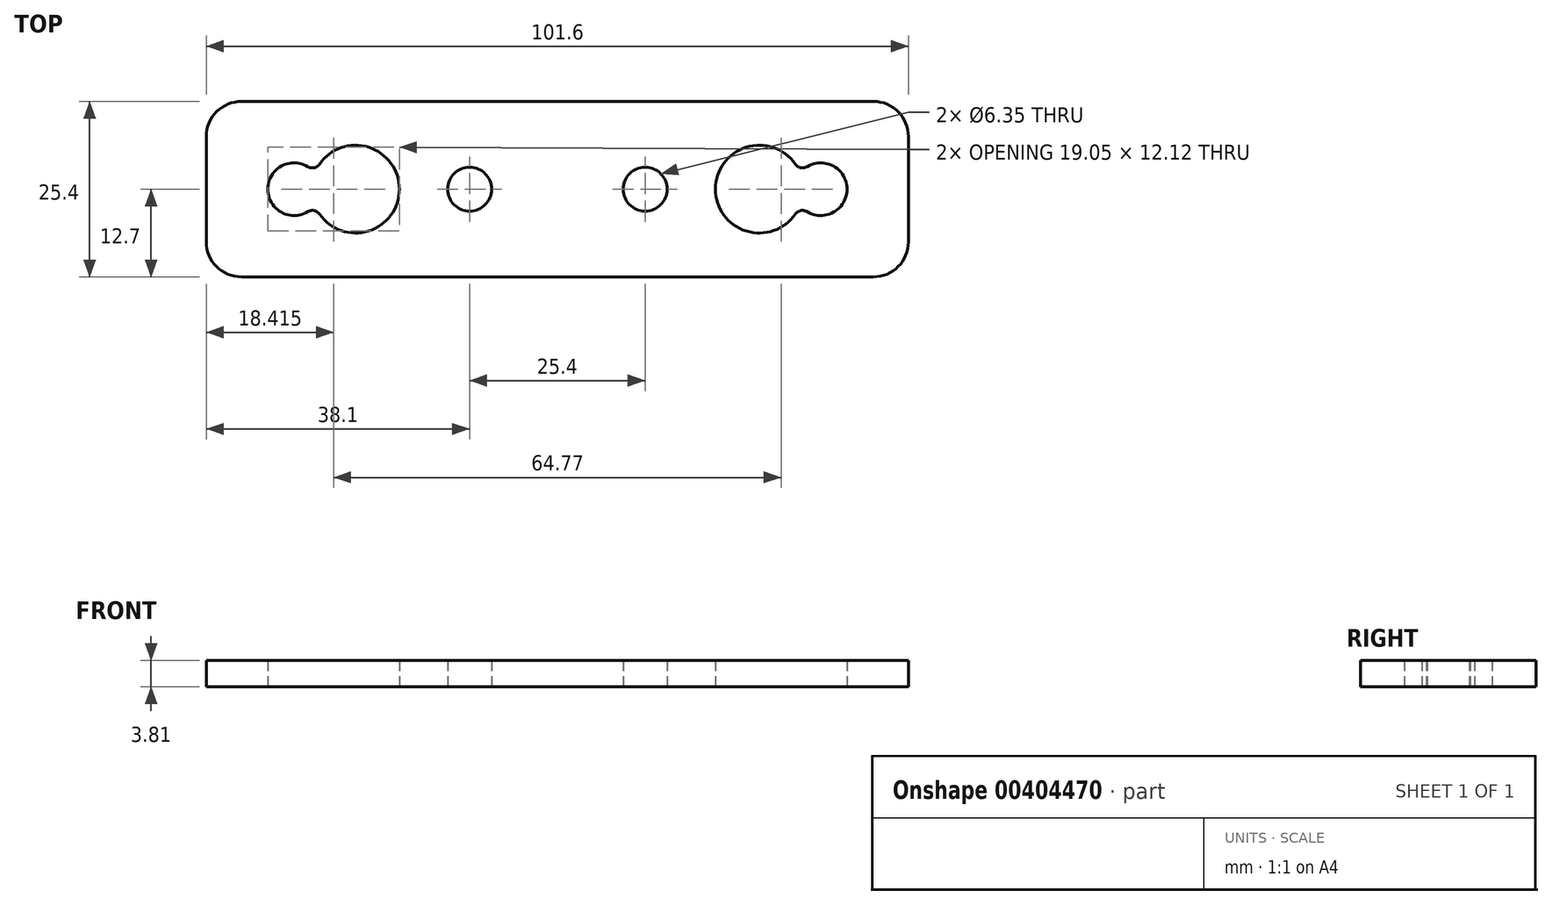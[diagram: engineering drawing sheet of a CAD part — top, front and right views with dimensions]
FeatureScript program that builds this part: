
annotation { "Feature Type Name" : "Feature", "Feature Type Description" : "" }
export const myFeature = defineFeature(function(context is Context, id is Id, definition is map)
    precondition{}
    {
        {
            var Q0;
            Q0=qCreatedBy(makeId("Top.planeOp"),FACE);
            var sketch = newSketch(context, id + "F0", { "sketchPlane" : qUnion([Q0])});
            skLineSegment(sketch, "E0.bottom", {"start": v(-50.8, 12.7) * mm, "end": v(50.8, 12.7) * mm});
            skLineSegment(sketch, "E0.top", {"start": v(-50.8, -12.7) * mm, "end": v(50.8, -12.7) * mm});
            skLineSegment(sketch, "E0.left", {"start": v(-50.8, 12.7) * mm, "end": v(-50.8, -12.7) * mm});
            skLineSegment(sketch, "E0.right", {"start": v(50.8, 12.7) * mm, "end": v(50.8, -12.7) * mm});
            skPoint(sketch, "E0.middle", {"position": v(0, 0) * mm});
            skLineSegment(sketch, "E1", {"start": v(-29.21, 0) * mm, "end": v(29.21, 0) * mm, "construction": true});
            skLineSegment(sketch, "E2", {"start": v(-38.1, 0) * mm, "end": v(38.1, 0) * mm, "construction": true});
            skArc(sketch, "E3", {"start": v(-35.1, 2.36) * mm, "mid": v(-35.56, 0) * mm, "end": v(-35.1, -2.36) * mm, "construction": true});
            skArc(sketch, "E4", {"start": v(-35.1, -2.36) * mm, "mid": v(-22.86, 0) * mm, "end": v(-35.1, 2.36) * mm});
            skArc(sketch, "E5", {"start": v(35.1, 2.36) * mm, "mid": v(22.86, 0) * mm, "end": v(35.1, -2.36) * mm});
            skArc(sketch, "E6", {"start": v(35.1, -2.36) * mm, "mid": v(35.56, 0) * mm, "end": v(35.1, 2.36) * mm, "construction": true});
            skArc(sketch, "E7", {"start": v(-35.1, 2.36) * mm, "mid": v(-41.91, 0) * mm, "end": v(-35.1, -2.36) * mm});
            skArc(sketch, "E8", {"start": v(-35.1, -2.36) * mm, "mid": v(-34.3, 0) * mm, "end": v(-35.1, 2.36) * mm, "construction": true});
            skArc(sketch, "E9", {"start": v(35.1, 2.36) * mm, "mid": v(34.3, 0) * mm, "end": v(35.1, -2.36) * mm, "construction": true});
            skArc(sketch, "E10", {"start": v(35.1, -2.36) * mm, "mid": v(41.91, 0) * mm, "end": v(35.1, 2.36) * mm});
            skCircle(sketch, "E11", {"center": v(-12.7, 0) * mm, "radius": 3.18 * mm});
            skCircle(sketch, "E12", {"center": v(12.7, 0) * mm, "radius": 3.18 * mm});
            skLineSegment(sketch, "E13", {"start": v(-12.7, 0) * mm, "end": v(12.7, 0) * mm, "construction": true});
            skSolve(sketch);
        }
        {
            var Q0;
            Q0 = qSketchRegion(id + "F0", true);
            extrude(context, id + "F1", {"entities" : qUnion([Q0]), "depth" : 3.8 * mm});
        }
        {
            var Q0;
            {var subQ0=sQuery(id+"F0.wireOp",EDGE,"E7");var subQ1=sQuery(id+"F0.wireOp",EDGE,"E4");Q0=makeQuery(id+"F1.opExtrude","SWEPT_EDGE",EDGE,{"disambiguationData":[OSD([subQ1,subQ0]),TDD([makeQuery(id+"F0.imprint","INTERSECT",VERTEX,{"disambiguationData":[OD(1.0)],"derivedFrom":[subQ1,subQ0]})])]});}
            var Q1;
            {var subQ0=sQuery(id+"F0.wireOp",EDGE,"E7");var subQ1=sQuery(id+"F0.wireOp",EDGE,"E4");Q1=makeQuery(id+"F1.opExtrude","SWEPT_EDGE",EDGE,{"disambiguationData":[OSD([subQ1,subQ0]),TDD([makeQuery(id+"F0.imprint","INTERSECT",VERTEX,{"disambiguationData":[OD(0.0)],"derivedFrom":[subQ1,subQ0]})])]});}
            var Q2;
            {var subQ0=sQuery(id+"F0.wireOp",EDGE,"E10");var subQ1=sQuery(id+"F0.wireOp",EDGE,"E5");Q2=makeQuery(id+"F1.opExtrude","SWEPT_EDGE",EDGE,{"disambiguationData":[OSD([subQ1,subQ0]),TDD([makeQuery(id+"F0.imprint","INTERSECT",VERTEX,{"disambiguationData":[OD(1.0)],"derivedFrom":[subQ1,subQ0]})])]});}
            var Q3;
            {var subQ0=sQuery(id+"F0.wireOp",EDGE,"E10");var subQ1=sQuery(id+"F0.wireOp",EDGE,"E5");Q3=makeQuery(id+"F1.opExtrude","SWEPT_EDGE",EDGE,{"disambiguationData":[OSD([subQ1,subQ0]),TDD([makeQuery(id+"F0.imprint","INTERSECT",VERTEX,{"disambiguationData":[OD(0.0)],"derivedFrom":[subQ1,subQ0]})])]});}
            fillet(context, id + "F2", {"entities" : qUnion([Q0, Q1, Q2, Q3]), "radius" : 1.27 * mm, "tangentPropagation" : true, "allowEdgeOverflow" : false});
        }
        {
            var Q0;
            Q0=makeQuery(id+"F1.opExtrude","SWEPT_EDGE",EDGE,{"disambiguationData":[OSD([sQuery(id+"F0.wireOp",EDGE,"E0.bottom"),sQuery(id+"F0.wireOp",EDGE,"E0.left")])]});
            var Q1;
            Q1=makeQuery(id+"F1.opExtrude","SWEPT_EDGE",EDGE,{"disambiguationData":[OSD([sQuery(id+"F0.wireOp",EDGE,"E0.top"),sQuery(id+"F0.wireOp",EDGE,"E0.left")])]});
            var Q2;
            Q2=makeQuery(id+"F1.opExtrude","SWEPT_EDGE",EDGE,{"disambiguationData":[OSD([sQuery(id+"F0.wireOp",EDGE,"E0.top"),sQuery(id+"F0.wireOp",EDGE,"E0.right")])]});
            var Q3;
            Q3=makeQuery(id+"F1.opExtrude","SWEPT_EDGE",EDGE,{"disambiguationData":[OSD([sQuery(id+"F0.wireOp",EDGE,"E0.bottom"),sQuery(id+"F0.wireOp",EDGE,"E0.right")])]});
            fillet(context, id + "F3", {"entities" : qUnion([Q0, Q1, Q2, Q3]), "radius" : 5.08 * mm, "tangentPropagation" : true, "allowEdgeOverflow" : false});
        }
    });
